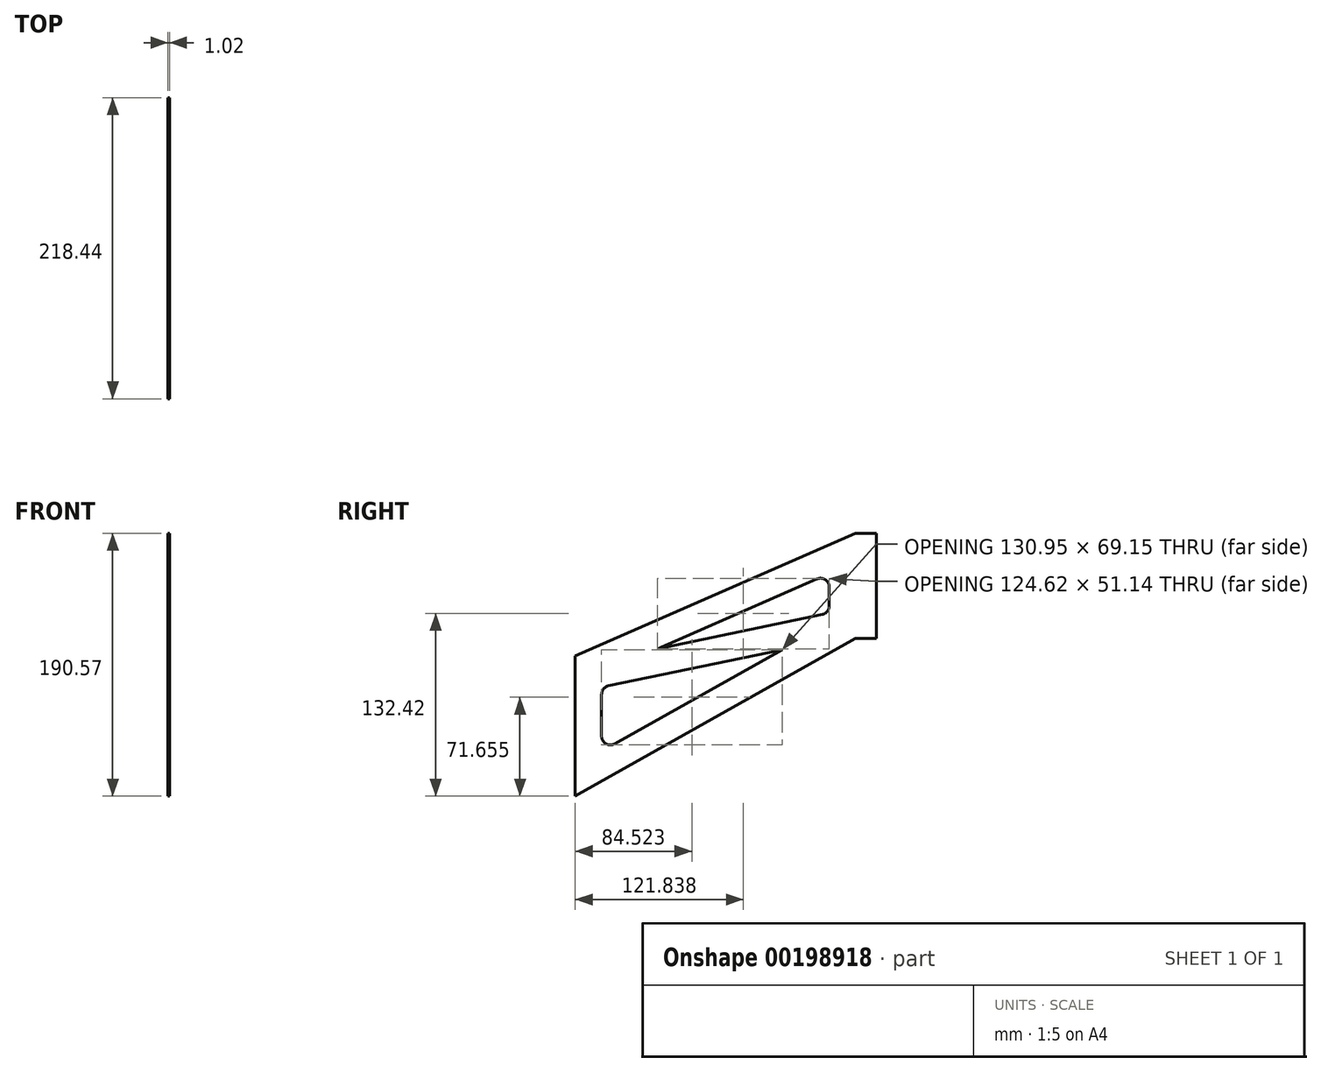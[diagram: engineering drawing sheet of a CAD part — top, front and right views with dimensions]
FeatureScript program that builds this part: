
annotation { "Feature Type Name" : "Feature", "Feature Type Description" : "" }
export const myFeature = defineFeature(function(context is Context, id is Id, definition is map)
    precondition{}
    {
        {
            var Q0;
            Q0=qCreatedBy(makeId("Right.planeOp"),FACE);
            var sketch = newSketch(context, id + "F0", { "sketchPlane" : qUnion([Q0])});
            skLineSegment(sketch, "E0", {"start": v(0, 0) * mm, "end": v(0, 101.6) * mm});
            skLineSegment(sketch, "E1", {"start": v(0, 101.6) * mm, "end": v(203.2, 190.5) * mm});
            skLineSegment(sketch, "E2", {"start": v(203.2, 190.5) * mm, "end": v(203.2, 114.3) * mm});
            skLineSegment(sketch, "E3", {"start": v(203.2, 114.3) * mm, "end": v(0, 0) * mm});
            skLineSegment(sketch, "E4", {"start": v(203.2, 114.3) * mm, "end": v(218.44, 114.3) * mm});
            skLineSegment(sketch, "E5", {"start": v(218.44, 190.57) * mm, "end": v(203.2, 190.5) * mm});
            skLineSegment(sketch, "E6", {"start": v(218.44, 114.3) * mm, "end": v(218.44, 190.57) * mm});
            skLineSegment(sketch, "E7", {"start": v(28.51, 37.9) * mm, "end": v(150, 106.23) * mm});
            skLineSegment(sketch, "E8", {"start": v(150, 106.23) * mm, "end": v(24.1, 80.01) * mm});
            skLineSegment(sketch, "E9", {"start": v(19.05, 73.8) * mm, "end": v(19.05, 43.43) * mm});
            skLineSegment(sketch, "E10", {"start": v(184.15, 137.96) * mm, "end": v(184.15, 151.66) * mm});
            skLineSegment(sketch, "E11", {"start": v(175.25, 157.48) * mm, "end": v(59.53, 106.85) * mm});
            skLineSegment(sketch, "E12", {"start": v(59.53, 106.85) * mm, "end": v(179.1, 131.75) * mm});
            skPoint(sketch, "E13.visualSharp", {"position": v(19.05, 78.96) * mm});
            skArc(sketch, "E13.filletArc", {"start": v(24.1, 80.01) * mm, "mid": v(20.47, 77.8) * mm, "end": v(19.05, 73.8) * mm});
            skPoint(sketch, "E14.visualSharp", {"position": v(19.05, 32.57) * mm});
            skArc(sketch, "E14.filletArc", {"start": v(19.05, 43.43) * mm, "mid": v(22.2, 37.95) * mm, "end": v(28.51, 37.9) * mm});
            skPoint(sketch, "E15.visualSharp", {"position": v(184.15, 132.8) * mm});
            skArc(sketch, "E15.filletArc", {"start": v(179.1, 131.75) * mm, "mid": v(182.73, 133.96) * mm, "end": v(184.15, 137.96) * mm});
            skPoint(sketch, "E16.visualSharp", {"position": v(184.15, 161.37) * mm});
            skArc(sketch, "E16.filletArc", {"start": v(184.15, 151.66) * mm, "mid": v(181.28, 156.98) * mm, "end": v(175.25, 157.48) * mm});
            skSolve(sketch);
        }
        {
            var Q0;
            Q0=makeQuery(id+"F0.imprint","IMPRINT",FACE,{"disambiguationData":[TD([[makeQuery(id+"F0.imprint","IMPRINT",EDGE,{"derivedFrom":sQuery(id+"F0.wireOp",EDGE,"E2")}),1.0]])]});
            var Q1;
            Q1=makeQuery(id+"F0.imprint","IMPRINT",FACE,{"disambiguationData":[TD([[makeQuery(id+"F0.imprint","IMPRINT",EDGE,{"derivedFrom":sQuery(id+"F0.wireOp",EDGE,"E0")}),-1.0]])]});
            extrude(context, id + "F1", {"entities" : qUnion([Q0, Q1]), "depth" : 1.02 * mm});
        }
    });
